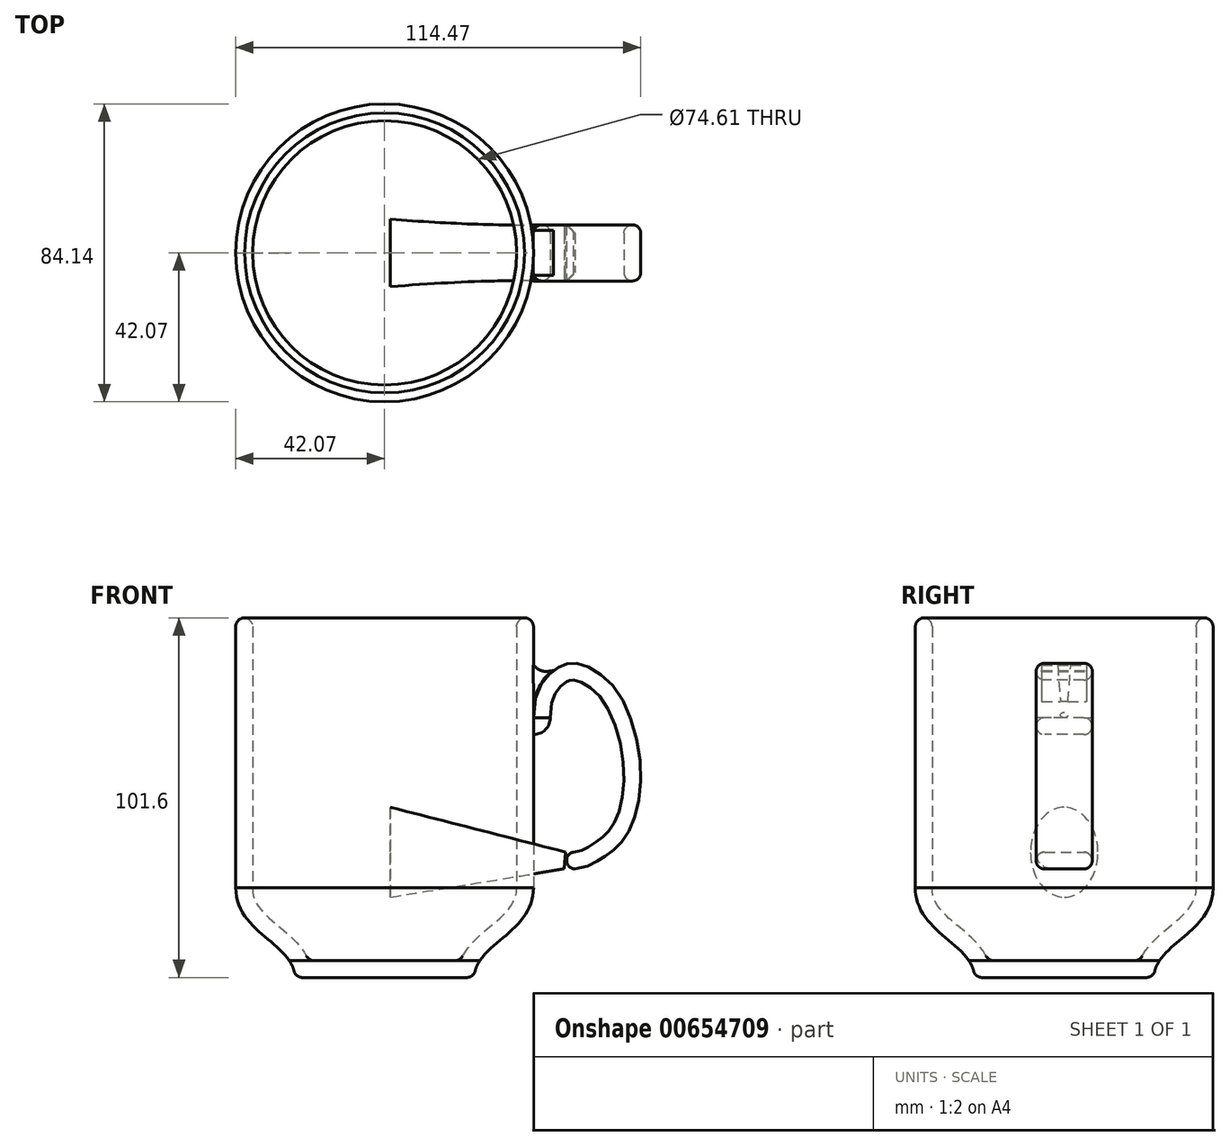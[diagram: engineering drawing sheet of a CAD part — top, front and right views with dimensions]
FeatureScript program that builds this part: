
annotation { "Feature Type Name" : "Feature", "Feature Type Description" : "" }
export const myFeature = defineFeature(function(context is Context, id is Id, definition is map)
    precondition{}
    {
        {
            var Q0;
            Q0=qCreatedBy(makeId("Front.planeOp"),FACE);
            var sketch = newSketch(context, id + "F0", { "sketchPlane" : qUnion([Q0])});
            skLineSegment(sketch, "E0", {"start": v(42.07, 47.32) * mm, "end": v(42.07, -28.88) * mm});
            skFitSpline(sketch, "E1", {"points": [v(42.07, -28.88) * mm, v(25.4, -54.28) * mm], "startDerivative": vector(0, -38.62) * mm, "endDerivative": vector(0, -28.68) * mm});
            skFitSpline(sketch, "E2.0", {"points": [v(37.3, -28.88) * mm, v(37.3, -29.43) * mm, v(37.22, -30.43) * mm, v(36.88, -31.75) * mm, v(36.34, -32.99) * mm, v(35.6, -34.21) * mm, v(34.63, -35.44) * mm, v(33.08, -37.09) * mm, v(30.7, -39.18) * mm, v(28.04, -41.37) * mm, v(25.92, -43.33) * mm, v(24.37, -44.95) * mm, v(22.93, -46.81) * mm, v(21.7, -48.98) * mm, v(20.85, -51.49) * mm, v(20.64, -53.34) * mm, v(20.64, -54.28) * mm]});
            skLineSegment(sketch, "E2.1", {"start": v(37.3, 47.32) * mm, "end": v(37.3, -28.88) * mm});
            skLineSegment(sketch, "E3", {"start": v(20.64, -54.28) * mm, "end": v(25.4, -54.28) * mm});
            skLineSegment(sketch, "E4", {"start": v(25.4, -54.28) * mm, "end": v(0, -54.28) * mm});
            skLineSegment(sketch, "E5", {"start": v(0, -54.28) * mm, "end": v(0, -49.52) * mm});
            skLineSegment(sketch, "E6", {"start": v(0, -49.52) * mm, "end": v(26.92, -49.52) * mm});
            skLineSegment(sketch, "E7", {"start": v(37.3, 47.32) * mm, "end": v(42.07, 47.32) * mm});
            skSolve(sketch);
        }
        {
            var Q0;
            {var subQ5=sQuery(id+"F0.wireOp",EDGE,"E0");Q0=makeQuery(id+"F0.imprint","IMPRINT",FACE,{"disambiguationData":[TD([[makeQuery(id+"F0.imprint","IMPRINT",EDGE,{"derivedFrom":subQ5}),-1.0]])]});}
            var Q1;
            {var subQ5=sQuery(id+"F0.wireOp",EDGE,"E5");Q1=makeQuery(id+"F0.imprint","IMPRINT",FACE,{"disambiguationData":[TD([[makeQuery(id+"F0.imprint","IMPRINT",EDGE,{"derivedFrom":subQ5}),-1.0]])]});}
            var Q2;
            {var subQ0=sQuery(id+"F0.wireOp",EDGE,"E4");var subQ1=sQuery(id+"F0.wireOp",EDGE,"E1");var subQ2=makeQuery(id+"F0.imprint","INTERSECT",VERTEX,{"derivedFrom":[subQ1,subQ0]});Q2=makeQuery(id+"F0.imprint","IMPRINT",FACE,{"disambiguationData":[TD([[makeQuery(id+"F0.imprint","IMPRINT",EDGE,{"disambiguationData":[TD([[subQ2,1.0]])],"derivedFrom":subQ1}),-1.0]])]});}
            var Q3;
            Q3=sQuery(id+"F0.wireOp",EDGE,"E5");
            revolve(context, id + "F1", {"entities" : qUnion([Q0, Q1, Q2]), "axis" : qUnion([Q3]), "revolveType" : RevolveType.FULL});
        }
        {
            var Q0;
            Q0=makeQuery(id+"F1.opRevolve","SWEPT_EDGE",EDGE,{"disambiguationData":[OSD([sQuery(id+"F0.wireOp",EDGE,"E0"),sQuery(id+"F0.wireOp",EDGE,"E7")])]});
            fillet(context, id + "F2", {"entities" : qUnion([Q0]), "radius" : 2.54 * mm, "tangentPropagation" : true, "allowEdgeOverflow" : false});
        }
        {
            var Q0;
            Q0=makeQuery(id+"F1.opRevolve","SWEPT_EDGE",EDGE,{"disambiguationData":[OSD([sQuery(id+"F0.wireOp",EDGE,"E2.1"),sQuery(id+"F0.wireOp",EDGE,"E7")])]});
            fillet(context, id + "F3", {"entities" : qUnion([Q0]), "radius" : 2.54 * mm, "tangentPropagation" : true, "allowEdgeOverflow" : false});
        }
        {
            var Q0;
            Q0=makeQuery(id+"F1.opRevolve","SWEPT_FACE",FACE,{"disambiguationData":[OSD([sQuery(id+"F0.wireOp",EDGE,"E6")])]});
            fillet(context, id + "F4", {"entities" : qUnion([Q0]), "radius" : 2.54 * mm, "tangentPropagation" : true, "allowEdgeOverflow" : false});
        }
        {
            var Q0;
            Q0=qCreatedBy(makeId("Right.planeOp"),FACE);
            cPlane(context, id + "F5", {"entities" : qUnion([Q0]), "cplaneType" : CPlaneType.OFFSET, "offset" : ((3 + (5 / 16)) / 2) * mm, "width" : 152.4 * mm, "height" : 152.4 * mm});
        }
        {
            var Q0;
            Q0=qCreatedBy(makeId("Front.planeOp"),FACE);
            var sketch = newSketch(context, id + "F6", { "sketchPlane" : qUnion([Q0])});
            skFitSpline(sketch, "E8", {"points": [v(42.07, 19.1) * mm, v(47.98, 32.64) * mm, v(54, 34.44) * mm, v(65.42, 26.92) * mm, v(72.34, 0) * mm, v(66.93, -16.1) * mm, v(60.9, -20.9) * mm, v(50.98, -23.61) * mm], "startDerivative": vector(-4.93, 145.2) * mm, "endDerivative": vector(-130.32, 6.86) * mm});
            skLineSegment(sketch, "E9", {"start": v(50.98, -23.61) * mm, "end": v(42.07, -23.61) * mm});
            skSolve(sketch);
        }
        {
            var Q0;
            Q0=qCreatedBy(makeId("Top.planeOp"),FACE);
            var Q1;
            Q1=sQuery(id+"F6.wireOp",VERTEX,"E8.0.internal");
            cPlane(context, id + "F7", {"entities" : qUnion([Q0, Q1]), "cplaneType" : CPlaneType.PLANE_POINT, "offset" : 25.4 * mm, "width" : 152.4 * mm, "height" : 152.4 * mm});
        }
        {
            var Q0;
            Q0=qCreatedBy(id+"F7.planeOp",FACE);
            var sketch = newSketch(context, id + "F8", { "sketchPlane" : qUnion([Q0])});
            skLineSegment(sketch, "E10.left", {"start": v(46.83, 5.56) * mm, "end": v(46.83, -5.56) * mm});
            skLineSegment(sketch, "E10.right", {"start": v(42.07, 5.56) * mm, "end": v(42.07, -5.56) * mm});
            skPoint(sketch, "E10.middle", {"position": v(44.45, 0) * mm});
            skArc(sketch, "E11", {"start": v(42.07, -5.56) * mm, "mid": v(44.45, -7.94) * mm, "end": v(46.83, -5.56) * mm});
            skArc(sketch, "E12", {"start": v(46.83, 5.56) * mm, "mid": v(44.45, 7.94) * mm, "end": v(42.07, 5.56) * mm});
            skPoint(sketch, "E13.orphan", {"position": v(42.07, 7.94) * mm});
            skPoint(sketch, "E14.orphan", {"position": v(46.83, 7.94) * mm});
            skPoint(sketch, "E15.orphan", {"position": v(42.07, -7.94) * mm});
            skPoint(sketch, "E16.orphan", {"position": v(46.83, -7.94) * mm});
            skSolve(sketch);
        }
        {
            var Q0;
            Q0=makeQuery(id+"F8.imprint","IMPRINT",FACE,{"disambiguationData":[TD([[makeQuery(id+"F8.imprint","IMPRINT",EDGE,{"derivedFrom":sQuery(id+"F8.wireOp",EDGE,"E10.left")}),-1.0]])]});
            var Q1;
            Q1=sQuery(id+"F6.wireOp",EDGE,"E8");
            sweep(context, id + "F9", {"operationType" : NewBodyOperationType.ADD, "profiles" : qUnion([Q0]), "path" : qUnion([Q1])});
        }
        {
            var Q0;
            Q0=qCreatedBy(makeId("Front.planeOp"),FACE);
            var sketch = newSketch(context, id + "F10", { "sketchPlane" : qUnion([Q0])});
            skFitSpline(sketch, "E17", {"points": [v(42.03, 34) * mm, v(48.45, 32.64) * mm], "startDerivative": vector(5.92, -6.66) * mm, "endDerivative": vector(8.14, 2.22) * mm});
            skLineSegment(sketch, "E18.0.0", {"start": v(51.4, -18.87) * mm, "end": v(50.98, -23.61) * mm});
            skFitSpline(sketch, "E18.0.1", {"points": [v(50.98, -23.61) * mm, v(53.72, -23.76) * mm, v(55.63, -23.45) * mm, v(57.89, -22.66) * mm, v(58.54, -22.34) * mm, v(59.77, -21.65) * mm, v(60.33, -21.27) * mm, v(61.91, -20.27) * mm, v(62.94, -19.63) * mm, v(64.98, -18.12) * mm, v(65.99, -17.23) * mm, v(68.32, -14.4) * mm, v(69.58, -12.13) * mm, v(71.5, -6.7) * mm, v(72.15, -3.52) * mm, v(72.59, 4.5) * mm, v(72.08, 9.56) * mm, v(70.3, 16.72) * mm, v(69.55, 19.03) * mm, v(67.72, 23.3) * mm, v(66.64, 25.25) * mm, v(63.7, 29.26) * mm, v(61.7, 31.04) * mm, v(57.7, 33.53) * mm, v(55.7, 34.24) * mm, v(52.83, 34.58) * mm, v(51.8, 34.49) * mm, v(49.86, 33.87) * mm, v(48.93, 33.35) * mm, v(46.51, 31.54) * mm, v(44.97, 29.98) * mm, v(42.69, 25.6) * mm, v(41.94, 22.76) * mm, v(42.07, 19.1) * mm]});
            skLineSegment(sketch, "E19", {"start": v(42.03, 34) * mm, "end": v(42.07, 19.1) * mm});
            skSolve(sketch);
        }
        {
            var Q0;
            {var subQ0=sQuery(id+"F10.wireOp",EDGE,"E17");Q0=makeQuery(id+"F10.imprint","IMPRINT",FACE,{"disambiguationData":[TD([[makeQuery(id+"F10.imprint","IMPRINT",EDGE,{"derivedFrom":subQ0}),-1.0]])]});}
            extrude(context, id + "F11", {"entities" : qUnion([Q0]), "operationType" : NewBodyOperationType.ADD, "depth" : 12.7 * mm, "offsetDistance" : 25.4 * mm, "symmetric" : true});
        }
        {
            var Q0;
            Q0=makeQuery(id+"F1.opRevolve","SWEPT_FACE",FACE,{"disambiguationData":[OSD([sQuery(id+"F0.wireOp",EDGE,"E4")])]});
            fillet(context, id + "F12", {"entities" : qUnion([Q0]), "radius" : 2.54 * mm, "tangentPropagation" : true, "allowEdgeOverflow" : false});
        }
        {
            var Q0;
            Q0=makeQuery(id+"F9.opSweep","CAP_FACE",FACE,{"disambiguationData":[OSD([sQuery(id+"F6.wireOp",VERTEX,"E8.start"),sQuery(id+"F8.wireOp",EDGE,"E10.left"),sQuery(id+"F8.wireOp",EDGE,"E10.right"),sQuery(id+"F8.wireOp",EDGE,"E11"),sQuery(id+"F8.wireOp",EDGE,"E12")])],"isStart":true});
            var sketch = newSketch(context, id + "F13", { "sketchPlane" : qUnion([Q0])});
            skLineSegment(sketch, "E20.3", {"start": v(42.03, 0) * mm, "end": v(42.07, 0) * mm});
            skLineSegment(sketch, "E20.5", {"start": v(46.83, -5.56) * mm, "end": v(46.83, 5.56) * mm});
            skLineSegment(sketch, "E20.6", {"start": v(42.07, -5.56) * mm, "end": v(42.07, 5.56) * mm});
            skPoint(sketch, "E20.7", {"position": v(44.45, 0) * mm});
            skArc(sketch, "E20.8", {"start": v(42.07, 5.56) * mm, "mid": v(44.45, 7.94) * mm, "end": v(46.83, 5.56) * mm});
            skArc(sketch, "E20.9", {"start": v(46.83, -5.56) * mm, "mid": v(44.45, -7.94) * mm, "end": v(42.07, -5.56) * mm});
            skPoint(sketch, "E20.10", {"position": v(42.07, -7.94) * mm});
            skPoint(sketch, "E20.11", {"position": v(46.83, -7.94) * mm});
            skPoint(sketch, "E20.12", {"position": v(42.07, 7.94) * mm});
            skPoint(sketch, "E20.13", {"position": v(46.83, 7.94) * mm});
            skSolve(sketch);
        }
        {
            var Q0;
            Q0=qCreatedBy(makeId("Front.planeOp"),FACE);
            var sketch = newSketch(context, id + "F14", { "sketchPlane" : qUnion([Q0])});
            skArc(sketch, "E21", {"start": v(44.45, 19.1) * mm, "mid": v(43.77, 17.43) * mm, "end": v(42.1, 16.72) * mm});
            skSolve(sketch);
        }
        {
            var Q0;
            Q0 = qSketchRegion(id + "F13", true);
            var Q1;
            Q1 = qConstructionFilter(qBodyType(qCreatedBy(id + "F14" ,EDGE), BodyType.WIRE), ConstructionObject.NO);
            sweep(context, id + "F15", {"operationType" : NewBodyOperationType.ADD, "profiles" : qUnion([Q0]), "path" : qUnion([Q1])});
        }
        {
            var Q0;
            Q0=makeQuery(id+"F9.opSweep","CAP_FACE",FACE,{"disambiguationData":[OSD([sQuery(id+"F6.wireOp",VERTEX,"E8.end"),sQuery(id+"F8.wireOp",EDGE,"E10.left"),sQuery(id+"F8.wireOp",EDGE,"E10.right"),sQuery(id+"F8.wireOp",EDGE,"E11"),sQuery(id+"F8.wireOp",EDGE,"E12")])],"isStart":false});
            cPlane(context, id + "F16", {"entities" : qUnion([Q0]), "cplaneType" : CPlaneType.OFFSET, "offset" : 0.25 * mm, "width" : 152.4 * mm, "height" : 152.4 * mm});
        }
        {
            var Q0;
            Q0=qCreatedBy(id+"F16.planeOp",FACE);
            var sketch = newSketch(context, id + "F17", { "sketchPlane" : qUnion([Q0])});
            skArc(sketch, "E22.0.0", {"start": v(-5.56, -14.36) * mm, "mid": v(-7.94, -16.74) * mm, "end": v(-5.56, -19.12) * mm});
            skLineSegment(sketch, "E22.0.1", {"start": v(-5.56, -19.12) * mm, "end": v(5.56, -19.12) * mm});
            skArc(sketch, "E22.0.2", {"start": v(5.56, -19.12) * mm, "mid": v(7.94, -16.74) * mm, "end": v(5.56, -14.36) * mm});
            skLineSegment(sketch, "E22.0.3", {"start": v(5.56, -14.36) * mm, "end": v(-5.56, -14.36) * mm});
            skSolve(sketch);
        }
        {
            var Q0;
            Q0=qCreatedBy(id+"F5.planeOp",FACE);
            var sketch = newSketch(context, id + "F18", { "sketchPlane" : qUnion([Q0])});
            skEllipse(sketch, "E23", {"center": v(0, -18.9) * mm, "majorRadius": 12.7 * mm, "minorRadius": 9.53 * mm, "majorAxis": v(0, -1)});
            skSolve(sketch);
        }
        {
            var Q0;
            Q0=qCreatedBy(makeId("Front.planeOp"),FACE);
            var sketch = newSketch(context, id + "F19", { "sketchPlane" : qUnion([Q0])});
            skLineSegment(sketch, "E24.0", {"start": v(42.07, -6.2) * mm, "end": v(42.07, -31.6) * mm, "construction": true});
            skLineSegment(sketch, "E25.0.3", {"start": v(51.4, -18.87) * mm, "end": v(50.98, -23.61) * mm});
            skFitSpline(sketch, "E26.0.4", {"points": [v(51.4, -18.87) * mm, v(53.7, -18.97) * mm, v(54.85, -18.7) * mm, v(56.15, -18.21) * mm, v(56.52, -18.02) * mm, v(57.38, -17.52) * mm, v(57.87, -17.2) * mm, v(59.54, -16.14) * mm, v(60.46, -15.56) * mm, v(62.04, -14.36) * mm, v(62.72, -13.74) * mm, v(64.3, -11.76) * mm, v(65.32, -9.96) * mm, v(66.88, -5.4) * mm, v(67.44, -2.66) * mm, v(67.8, 4.37) * mm, v(67.32, 9.03) * mm, v(65.7, 15.5) * mm, v(65, 17.58) * mm, v(63.39, 21.3) * mm, v(62.46, 22.94) * mm, v(60.12, 26.07) * mm, v(58.55, 27.42) * mm, v(55.56, 29.23) * mm, v(54.13, 29.66) * mm, v(52.68, 29.78) * mm, v(52.43, 29.71) * mm, v(51.79, 29.46) * mm, v(51.35, 29.23) * mm, v(49.7, 27.95) * mm, v(48.71, 26.92) * mm, v(47.25, 23.98) * mm, v(46.7, 22.03) * mm, v(46.83, 19.1) * mm]});
            skLineSegment(sketch, "E26.0.5", {"start": v(42.07, 19.1) * mm, "end": v(46.83, 19.1) * mm});
            skCircle(sketch, "E27", {"center": v(50.75, -9.6) * mm, "radius": 6.66 * mm});
            skSolve(sketch);
        }
        {
            var Q0;
            Q0=qCreatedBy(makeId("Front.planeOp"),FACE);
            var sketch = newSketch(context, id + "F20", { "sketchPlane" : qUnion([Q0])});
            skLineSegment(sketch, "E28", {"start": v(53.81, -23.6) * mm, "end": v(53.81, -18.82) * mm, "construction": true});
            skLineSegment(sketch, "E29", {"start": v(50.83, -18.82) * mm, "end": v(53.81, -18.82) * mm});
            skLineSegment(sketch, "E30", {"start": v(50.83, -18.82) * mm, "end": v(50.83, -24.04) * mm});
            skLineSegment(sketch, "E31", {"start": v(53.81, -23.6) * mm, "end": v(50.83, -24.04) * mm});
            skArc(sketch, "E32", {"start": v(53.81, -18.82) * mm, "mid": v(51.43, -21.2) * mm, "end": v(53.81, -23.6) * mm});
            skSolve(sketch);
        }
        {
            var Q0;
            Q0 = qSketchRegion(id + "F20", true);
            extrude(context, id + "F21", {"entities" : qUnion([Q0]), "operationType" : NewBodyOperationType.REMOVE, "oppositeDirection" : true, "depth" : 25.4 * mm, "offsetDistance" : 25.4 * mm, "symmetric" : true});
        }
        {
            var Q1;
            Q1 = qSketchRegion(id + "F17", true);
            var Q2;
            Q2 = qSketchRegion(id + "F18", true);
            loft(context, id + "F22", {"sheetProfilesArray" : [{ "sheetProfileEntities" : qUnion([Q1]) }, { "sheetProfileEntities" : qUnion([Q2]) }]});
        }
    });
